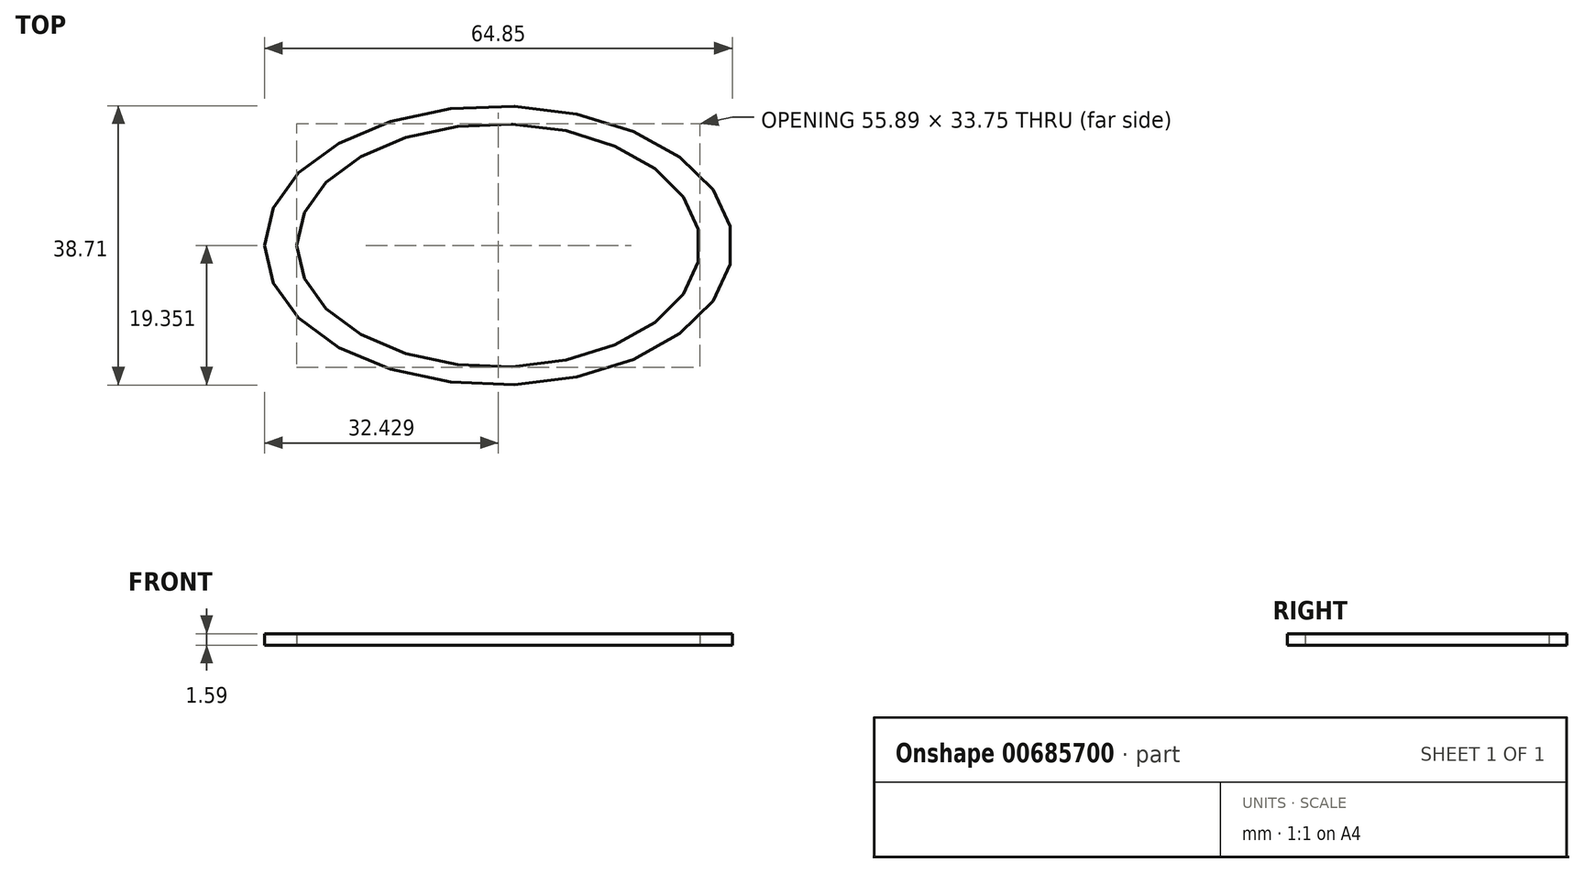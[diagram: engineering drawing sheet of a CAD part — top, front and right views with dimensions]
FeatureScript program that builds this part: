
annotation { "Feature Type Name" : "Feature", "Feature Type Description" : "" }
export const myFeature = defineFeature(function(context is Context, id is Id, definition is map)
    precondition{}
    {
        {
            var Q0;
            Q0=qCreatedBy(makeId("Top.planeOp"),FACE);
            var sketch = newSketch(context, id + "F0", { "sketchPlane" : qUnion([Q0])});
            skEllipse(sketch, "E0", {"center": v(38.58, -38.13) * mm, "majorRadius": 27.94 * mm, "minorRadius": 16.88 * mm, "majorAxis": v(-1, 0)});
            skEllipse(sketch, "E1", {"center": v(38.58, -38.13) * mm, "majorRadius": 32.42 * mm, "minorRadius": 19.36 * mm, "majorAxis": v(-1, 0)});
            skSolve(sketch);
        }
        {
            var Q0;
            Q0=makeQuery(id+"F0.imprint","IMPRINT",FACE,{"disambiguationData":[TD([[makeQuery(id+"F0.imprint","IMPRINT",EDGE,{"derivedFrom":sQuery(id+"F0.wireOp",EDGE,"E0")}),-1.0]])]});
            extrude(context, id + "F1", {"entities" : qUnion([Q0]), "depth" : 1.59 * mm, "offsetDistance" : 25.4 * mm});
        }
    });
